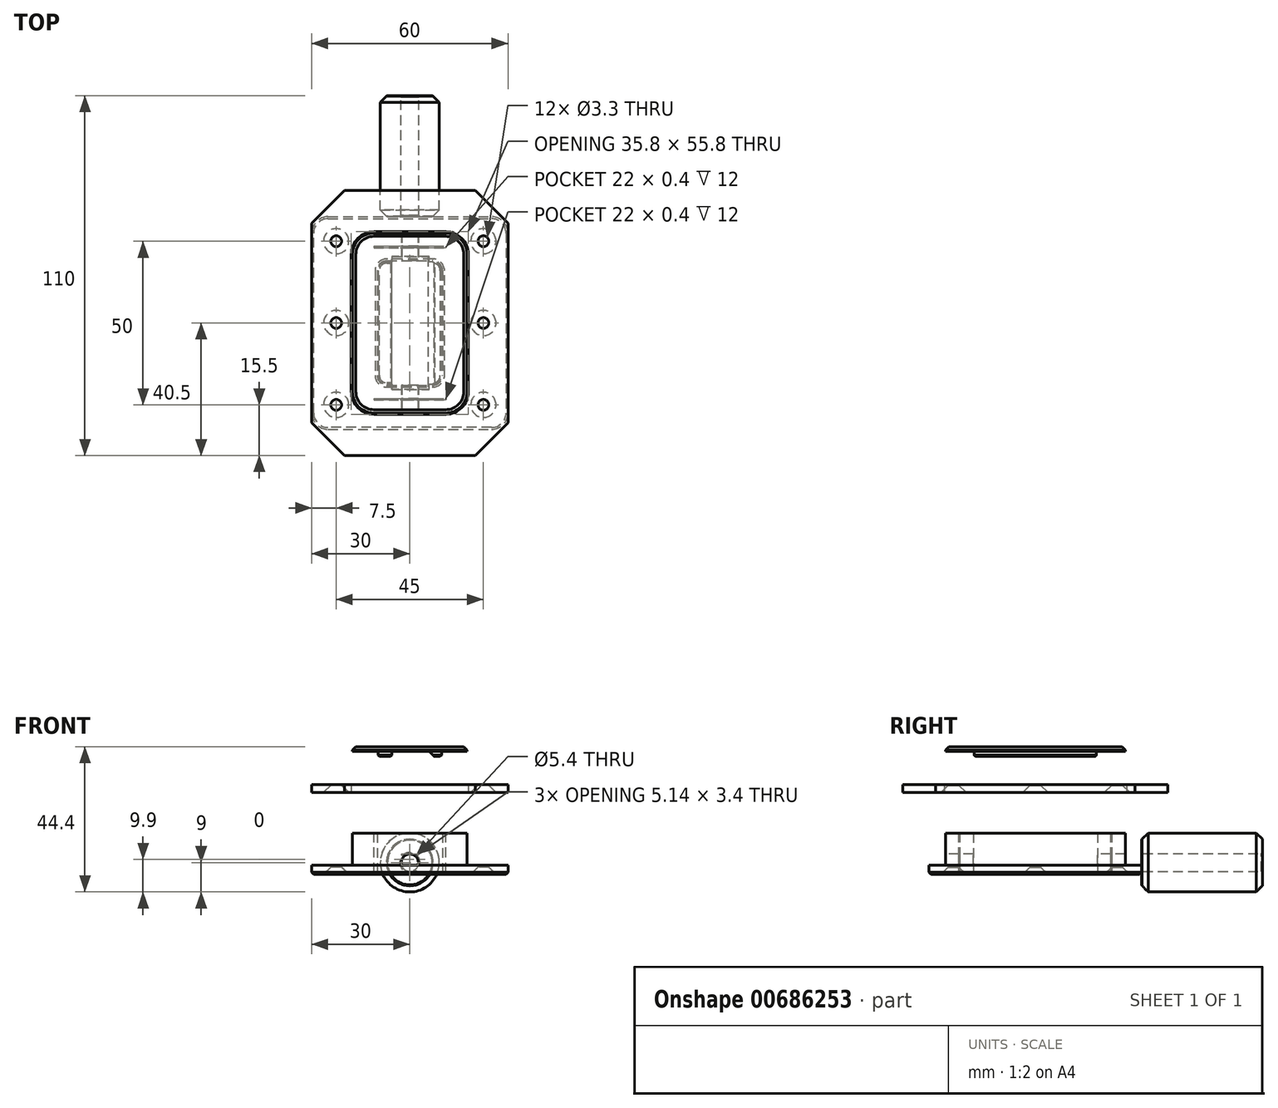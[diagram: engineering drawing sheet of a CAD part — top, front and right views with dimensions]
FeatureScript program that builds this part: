
annotation { "Feature Type Name" : "Feature", "Feature Type Description" : "" }
export const myFeature = defineFeature(function(context is Context, id is Id, definition is map)
    precondition{}
    {
        {
            var Q0;
            Q0=qCreatedBy(makeId("Top.planeOp"),FACE);
            cPlane(context, id + "F0", {"entities" : qUnion([Q0]), "cplaneType" : CPlaneType.OFFSET, "offset" : 25 * mm, "width" : 150 * mm, "height" : 150 * mm});
        }
        {
            var Q0;
            Q0=qCreatedBy(makeId("Top.planeOp"),FACE);
            var sketch = newSketch(context, id + "F1", { "sketchPlane" : qUnion([Q0])});
            skLineSegment(sketch, "E0.bottom", {"start": v(-25, 32.5) * mm, "end": v(25, 32.5) * mm});
            skLineSegment(sketch, "E0.top", {"start": v(-25, -32.5) * mm, "end": v(25, -32.5) * mm});
            skLineSegment(sketch, "E0.left", {"start": v(-30, 27.5) * mm, "end": v(-30, -27.5) * mm});
            skLineSegment(sketch, "E0.right", {"start": v(30, 27.5) * mm, "end": v(30, -27.5) * mm});
            skPoint(sketch, "E1.visualSharp", {"position": v(-30, 32.5) * mm});
            skArc(sketch, "E1.filletArc", {"start": v(-25, 32.5) * mm, "mid": v(-28.54, 31.04) * mm, "end": v(-30, 27.5) * mm});
            skPoint(sketch, "E2.visualSharp", {"position": v(30, 32.5) * mm});
            skArc(sketch, "E2.filletArc", {"start": v(30, 27.5) * mm, "mid": v(28.54, 31.04) * mm, "end": v(25, 32.5) * mm});
            skPoint(sketch, "E3.visualSharp", {"position": v(-30, -32.5) * mm});
            skArc(sketch, "E3.filletArc", {"start": v(-30, -27.5) * mm, "mid": v(-28.54, -31.04) * mm, "end": v(-25, -32.5) * mm});
            skPoint(sketch, "E4.visualSharp", {"position": v(30, -32.5) * mm});
            skArc(sketch, "E4.filletArc", {"start": v(25, -32.5) * mm, "mid": v(28.54, -31.04) * mm, "end": v(30, -27.5) * mm});
            skLineSegment(sketch, "E5.bottom", {"start": v(-7, 19) * mm, "end": v(7, 19) * mm});
            skLineSegment(sketch, "E5.top", {"start": v(-7, -19) * mm, "end": v(7, -19) * mm});
            skLineSegment(sketch, "E5.left", {"start": v(-10, 16) * mm, "end": v(-10, -16) * mm});
            skLineSegment(sketch, "E5.right", {"start": v(10, 16) * mm, "end": v(10, -16) * mm});
            skLineSegment(sketch, "E6", {"start": v(0, 19) * mm, "end": v(0, 32.5) * mm, "construction": true});
            skLineSegment(sketch, "E7", {"start": v(0, -19) * mm, "end": v(0, -32.5) * mm, "construction": true});
            skPoint(sketch, "E8.visualSharp", {"position": v(-10, 19) * mm});
            skArc(sketch, "E8.filletArc", {"start": v(-7, 19) * mm, "mid": v(-9.12, 18.12) * mm, "end": v(-10, 16) * mm});
            skPoint(sketch, "E9.visualSharp", {"position": v(10, 19) * mm});
            skArc(sketch, "E9.filletArc", {"start": v(10, 16) * mm, "mid": v(9.12, 18.12) * mm, "end": v(7, 19) * mm});
            skPoint(sketch, "E10.visualSharp", {"position": v(10, -19) * mm});
            skArc(sketch, "E10.filletArc", {"start": v(7, -19) * mm, "mid": v(9.12, -18.12) * mm, "end": v(10, -16) * mm});
            skPoint(sketch, "E11.visualSharp", {"position": v(-10, -19) * mm});
            skArc(sketch, "E11.filletArc", {"start": v(-10, -16) * mm, "mid": v(-9.12, -18.12) * mm, "end": v(-7, -19) * mm});
            skLineSegment(sketch, "E12", {"start": v(-30, 32.5) * mm, "end": v(30, -32.5) * mm, "construction": true});
            skLineSegment(sketch, "E13", {"start": v(30, 32.5) * mm, "end": v(-30, -32.5) * mm, "construction": true});
            skCircle(sketch, "E14", {"center": v(-22.5, 25) * mm, "radius": 1.65 * mm});
            skCircle(sketch, "E15", {"center": v(22.5, 25) * mm, "radius": 1.65 * mm});
            skCircle(sketch, "E16", {"center": v(22.5, -25) * mm, "radius": 1.65 * mm});
            skCircle(sketch, "E17", {"center": v(-22.5, -25) * mm, "radius": 1.65 * mm});
            skCircle(sketch, "E18", {"center": v(-22.5, 0) * mm, "radius": 1.65 * mm});
            skCircle(sketch, "E19", {"center": v(22.5, 0) * mm, "radius": 1.65 * mm});
            skLineSegment(sketch, "E20.bottom", {"start": v(-22.5, -25) * mm, "end": v(22.5, -25) * mm, "construction": true});
            skLineSegment(sketch, "E20.top", {"start": v(-22.5, 25) * mm, "end": v(22.5, 25) * mm, "construction": true});
            skLineSegment(sketch, "E20.left", {"start": v(-22.5, -25) * mm, "end": v(-22.5, 25) * mm, "construction": true});
            skLineSegment(sketch, "E20.right", {"start": v(22.5, -25) * mm, "end": v(22.5, 25) * mm, "construction": true});
            skLineSegment(sketch, "E21", {"start": v(-22.5, 0) * mm, "end": v(22.5, 0) * mm, "construction": true});
            skSolve(sketch);
        }
        {
            var Q0;
            Q0=makeQuery(id+"F1.imprint","IMPRINT",FACE,{"disambiguationData":[TD([[makeQuery(id+"F1.imprint","IMPRINT",EDGE,{"derivedFrom":sQuery(id+"F1.wireOp",EDGE,"E0.bottom")}),-1.0]])]});
            extrude(context, id + "F2", {"entities" : qUnion([Q0]), "depth" : 2.8 * mm, "offsetDistance" : 25 * mm});
        }
        {
            var Q0;
            Q0=makeQuery(id+"F2.opExtrude","CAP_FACE",FACE,{"disambiguationData":[OSD([sQuery(id+"F1.wireOp",EDGE,"E0.bottom"),sQuery(id+"F1.wireOp",EDGE,"E0.top"),sQuery(id+"F1.wireOp",EDGE,"E0.left"),sQuery(id+"F1.wireOp",EDGE,"E0.right"),sQuery(id+"F1.wireOp",EDGE,"E1.filletArc"),sQuery(id+"F1.wireOp",EDGE,"E2.filletArc"),sQuery(id+"F1.wireOp",EDGE,"E3.filletArc"),sQuery(id+"F1.wireOp",EDGE,"E4.filletArc")])],"isStart":false});
            var sketch = newSketch(context, id + "F3", { "sketchPlane" : qUnion([Q0])});
            skArc(sketch, "E22.0.0", {"start": v(-30, -27.5) * mm, "mid": v(-28.54, -31.04) * mm, "end": v(-25, -32.5) * mm, "construction": true});
            skLineSegment(sketch, "E22.0.1", {"start": v(-25, -32.5) * mm, "end": v(25, -32.5) * mm, "construction": true});
            skArc(sketch, "E22.0.2", {"start": v(25, -32.5) * mm, "mid": v(28.54, -31.04) * mm, "end": v(30, -27.5) * mm, "construction": true});
            skLineSegment(sketch, "E22.0.3", {"start": v(30, -27.5) * mm, "end": v(30, 27.5) * mm, "construction": true});
            skArc(sketch, "E22.0.4", {"start": v(30, 27.5) * mm, "mid": v(28.54, 31.04) * mm, "end": v(25, 32.5) * mm, "construction": true});
            skLineSegment(sketch, "E22.0.5", {"start": v(25, 32.5) * mm, "end": v(-25, 32.5) * mm, "construction": true});
            skArc(sketch, "E22.0.6", {"start": v(-25, 32.5) * mm, "mid": v(-28.54, 31.04) * mm, "end": v(-30, 27.5) * mm, "construction": true});
            skLineSegment(sketch, "E22.0.7", {"start": v(-30, 27.5) * mm, "end": v(-30, -27.5) * mm, "construction": true});
            skLineSegment(sketch, "E23.bottom", {"start": v(-11, 27.5) * mm, "end": v(11, 27.5) * mm});
            skLineSegment(sketch, "E23.top", {"start": v(-11, -27.5) * mm, "end": v(11, -27.5) * mm});
            skLineSegment(sketch, "E23.left", {"start": v(-17.5, 21) * mm, "end": v(-17.5, -21) * mm});
            skLineSegment(sketch, "E23.right", {"start": v(17.5, 21) * mm, "end": v(17.5, -21) * mm});
            skLineSegment(sketch, "E24", {"start": v(0, 32.5) * mm, "end": v(0, 27.5) * mm, "construction": true});
            skLineSegment(sketch, "E25", {"start": v(0, -27.5) * mm, "end": v(0, -32.5) * mm, "construction": true});
            skPoint(sketch, "E26.visualSharp", {"position": v(-17.5, 27.5) * mm});
            skArc(sketch, "E26.filletArc", {"start": v(-11, 27.5) * mm, "mid": v(-15.6, 25.6) * mm, "end": v(-17.5, 21) * mm});
            skPoint(sketch, "E27.visualSharp", {"position": v(17.5, 27.5) * mm});
            skArc(sketch, "E27.filletArc", {"start": v(17.5, 21) * mm, "mid": v(15.6, 25.6) * mm, "end": v(11, 27.5) * mm});
            skPoint(sketch, "E28.visualSharp", {"position": v(-17.5, -27.5) * mm});
            skArc(sketch, "E28.filletArc", {"start": v(-17.5, -21) * mm, "mid": v(-15.6, -25.6) * mm, "end": v(-11, -27.5) * mm});
            skPoint(sketch, "E29.visualSharp", {"position": v(17.5, -27.5) * mm});
            skArc(sketch, "E29.filletArc", {"start": v(11, -27.5) * mm, "mid": v(15.6, -25.6) * mm, "end": v(17.5, -21) * mm});
            skSolve(sketch);
        }
        {
            var Q0;
            Q0=makeQuery(id+"F3.imprint","IMPRINT",FACE,{"disambiguationData":[TD([[makeQuery(id+"F3.imprint","IMPRINT",EDGE,{"derivedFrom":sQuery(id+"F3.wireOp",EDGE,"E23.bottom")}),-1.0]])]});
            extrude(context, id + "F4", {"entities" : qUnion([Q0]), "operationType" : NewBodyOperationType.ADD, "depth" : 9.8 * mm, "offsetDistance" : 25 * mm});
        }
        {
            var Q0;
            Q0=makeQuery(id+"F2.opExtrude","SWEPT_FACE",FACE,{"disambiguationData":[OSD([sQuery(id+"F1.wireOp",EDGE,"E0.top")])]});
            var sketch = newSketch(context, id + "F5", { "sketchPlane" : qUnion([Q0])});
            skLineSegment(sketch, "E30.0.0", {"start": v(-11, 2.8) * mm, "end": v(11, 2.8) * mm, "construction": true});
            skLineSegment(sketch, "E30.0.1", {"start": v(11, 2.8) * mm, "end": v(11, 12.6) * mm, "construction": true});
            skLineSegment(sketch, "E30.0.2", {"start": v(11, 12.6) * mm, "end": v(-11, 12.6) * mm});
            skLineSegment(sketch, "E30.0.3", {"start": v(-11, 12.6) * mm, "end": v(-11, 2.8) * mm, "construction": true});
            skLineSegment(sketch, "E31", {"start": v(-11, 3.6) * mm, "end": v(11, 3.6) * mm});
            skCircle(sketch, "E32", {"center": v(0, 3.6) * mm, "radius": 2.6 * mm});
            skCircle(sketch, "E33", {"center": v(0, 3.6) * mm, "radius": 9 * mm, "construction": true});
            skSolve(sketch);
        }
        {
            var Q0;
            {var subQ0=sQuery(id+"F5.wireOp",EDGE,"E32");var subQ1=sQuery(id+"F5.wireOp",EDGE,"E31");var subQ2=makeQuery(id+"F5.imprint","INTERSECT",VERTEX,{"disambiguationData":[OD(0.0)],"derivedFrom":[subQ1,subQ0]});Q0=makeQuery(id+"F5.imprint","IMPRINT",FACE,{"disambiguationData":[TD([[makeQuery(id+"F5.imprint","IMPRINT",EDGE,{"disambiguationData":[TD([[subQ2,-1.0]])],"derivedFrom":subQ1}),1.0]])]});}
            var Q1;
            {var subQ0=sQuery(id+"F5.wireOp",EDGE,"E32");var subQ1=sQuery(id+"F5.wireOp",EDGE,"E31");var subQ2=makeQuery(id+"F5.imprint","INTERSECT",VERTEX,{"disambiguationData":[OD(0.0)],"derivedFrom":[subQ1,subQ0]});Q1=makeQuery(id+"F5.imprint","IMPRINT",FACE,{"disambiguationData":[TD([[makeQuery(id+"F5.imprint","IMPRINT",EDGE,{"disambiguationData":[TD([[subQ2,-1.0]])],"derivedFrom":subQ1}),-1.0]])]});}
            var Q2;
            {var subQ0=sQuery(id+"F5.wireOp",EDGE,"E32");var subQ1=makeQuery(id+"F2.opExtrude","CAP_EDGE",EDGE,{"disambiguationData":[OSD([sQuery(id+"F1.wireOp",EDGE,"E0.top")])],"isStart":false});var subQ2=makeQuery(id+"F5.imprint","INTERSECT",VERTEX,{"disambiguationData":[OD(0.0)],"derivedFrom":[subQ1,subQ0]});Q2=makeQuery(id+"F5.imprint","IMPRINT",FACE,{"disambiguationData":[TD([[makeQuery(id+"F5.imprint","IMPRINT",EDGE,{"disambiguationData":[TD([[subQ2,-1.0]])],"derivedFrom":subQ0}),1.0]])]});}
            var Q3;
            Q3=makeQuery(id+"F2.opExtrude","SWEPT_FACE",FACE,{"disambiguationData":[OSD([sQuery(id+"F1.wireOp",EDGE,"E0.bottom")])]});
            extrude(context, id + "F6", {"entities" : qUnion([Q0, Q1, Q2]), "operationType" : NewBodyOperationType.REMOVE, "endBound" : BoundingType.UP_TO_SURFACE, "oppositeDirection" : true, "depth" : 25 * mm, "endBoundEntityFace" : qUnion([Q3]), "offsetDistance" : 25 * mm});
        }
        {
            var Q0;
            Q0=qCreatedBy(id+"F0.planeOp",FACE);
            var sketch = newSketch(context, id + "F7", { "sketchPlane" : qUnion([Q0])});
            skArc(sketch, "E34.0", {"start": v(25, -32.5) * mm, "mid": v(28.54, -31.04) * mm, "end": v(30, -27.5) * mm, "construction": true});
            skLineSegment(sketch, "E35.0", {"start": v(30, 27.5) * mm, "end": v(30, -27.5) * mm, "construction": true});
            skLineSegment(sketch, "E36.0", {"start": v(-25, -32.5) * mm, "end": v(25, -32.5) * mm, "construction": true});
            skLineSegment(sketch, "E37.0", {"start": v(-30, 27.5) * mm, "end": v(-30, -27.5) * mm, "construction": true});
            skArc(sketch, "E38.0", {"start": v(-30, -27.5) * mm, "mid": v(-28.54, -31.04) * mm, "end": v(-25, -32.5) * mm, "construction": true});
            skArc(sketch, "E38.1", {"start": v(-25, 32.5) * mm, "mid": v(-28.54, 31.04) * mm, "end": v(-30, 27.5) * mm, "construction": true});
            skLineSegment(sketch, "E38.2", {"start": v(-25, 32.5) * mm, "end": v(25, 32.5) * mm, "construction": true});
            skArc(sketch, "E39.0", {"start": v(30, 27.5) * mm, "mid": v(28.54, 31.04) * mm, "end": v(25, 32.5) * mm, "construction": true});
            skCircle(sketch, "E40.0", {"center": v(22.5, -25) * mm, "radius": 1.65 * mm});
            skCircle(sketch, "E41.0", {"center": v(22.5, 0) * mm, "radius": 1.65 * mm});
            skCircle(sketch, "E42.0", {"center": v(22.5, 25) * mm, "radius": 1.65 * mm});
            skCircle(sketch, "E43.0", {"center": v(-22.5, 25) * mm, "radius": 1.65 * mm});
            skCircle(sketch, "E44.0", {"center": v(-22.5, 0) * mm, "radius": 1.65 * mm});
            skCircle(sketch, "E45.0", {"center": v(-22.5, -25) * mm, "radius": 1.65 * mm});
            skArc(sketch, "E46.0", {"start": v(11, -27.5) * mm, "mid": v(15.6, -25.6) * mm, "end": v(17.5, -21) * mm, "construction": true});
            skLineSegment(sketch, "E47.0", {"start": v(17.5, 21) * mm, "end": v(17.5, -21) * mm, "construction": true});
            skArc(sketch, "E48.0", {"start": v(17.5, 21) * mm, "mid": v(15.6, 25.6) * mm, "end": v(11, 27.5) * mm, "construction": true});
            skLineSegment(sketch, "E49.0", {"start": v(-11, 27.5) * mm, "end": v(11, 27.5) * mm, "construction": true});
            skArc(sketch, "E50.0", {"start": v(-11, 27.5) * mm, "mid": v(-15.6, 25.6) * mm, "end": v(-17.5, 21) * mm, "construction": true});
            skLineSegment(sketch, "E51.0", {"start": v(-17.5, 21) * mm, "end": v(-17.5, -21) * mm, "construction": true});
            skArc(sketch, "E52.0", {"start": v(-17.5, -21) * mm, "mid": v(-15.6, -25.6) * mm, "end": v(-11, -27.5) * mm, "construction": true});
            skLineSegment(sketch, "E53.0", {"start": v(-11, -27.5) * mm, "end": v(11, -27.5) * mm, "construction": true});
            skLineSegment(sketch, "E54.bottom", {"start": v(30, -40.5) * mm, "end": v(-30, -40.5) * mm});
            skLineSegment(sketch, "E54.top", {"start": v(30, 40.5) * mm, "end": v(-30, 40.5) * mm});
            skLineSegment(sketch, "E54.left", {"start": v(30, -40.5) * mm, "end": v(30, 40.5) * mm});
            skLineSegment(sketch, "E54.right", {"start": v(-30, -40.5) * mm, "end": v(-30, 40.5) * mm});
            skArc(sketch, "E55.0", {"start": v(-11, 27.9) * mm, "mid": v(-15.88, 25.88) * mm, "end": v(-17.9, 21) * mm});
            skLineSegment(sketch, "E55.1", {"start": v(-11, 27.9) * mm, "end": v(11, 27.9) * mm});
            skLineSegment(sketch, "E55.2", {"start": v(-17.9, 21) * mm, "end": v(-17.9, -21) * mm});
            skArc(sketch, "E55.3", {"start": v(17.9, 21) * mm, "mid": v(15.88, 25.88) * mm, "end": v(11, 27.9) * mm});
            skArc(sketch, "E55.4", {"start": v(-17.9, -21) * mm, "mid": v(-15.88, -25.88) * mm, "end": v(-11, -27.9) * mm});
            skLineSegment(sketch, "E55.5", {"start": v(-11, -27.9) * mm, "end": v(11, -27.9) * mm});
            skArc(sketch, "E55.6", {"start": v(11, -27.9) * mm, "mid": v(15.88, -25.88) * mm, "end": v(17.9, -21) * mm});
            skLineSegment(sketch, "E55.7", {"start": v(17.9, 21) * mm, "end": v(17.9, -21) * mm});
            skSolve(sketch);
        }
        {
            var Q0;
            Q0=makeQuery(id+"F7.imprint","IMPRINT",FACE,{"disambiguationData":[TD([[makeQuery(id+"F7.imprint","IMPRINT",EDGE,{"derivedFrom":sQuery(id+"F7.wireOp",EDGE,"E40.0")}),-1.0]])]});
            extrude(context, id + "F8", {"entities" : qUnion([Q0]), "depth" : 2.4 * mm, "offsetDistance" : 25 * mm});
        }
        {
            var Q0;
            Q0=makeQuery(id+"F8.opExtrude","SWEPT_EDGE",EDGE,{"disambiguationData":[OSD([sQuery(id+"F7.wireOp",EDGE,"E54.bottom"),sQuery(id+"F7.wireOp",EDGE,"E54.left")])]});
            var Q1;
            Q1=makeQuery(id+"F8.opExtrude","SWEPT_EDGE",EDGE,{"disambiguationData":[OSD([sQuery(id+"F7.wireOp",EDGE,"E54.top"),sQuery(id+"F7.wireOp",EDGE,"E54.left")])]});
            var Q2;
            Q2=makeQuery(id+"F8.opExtrude","SWEPT_EDGE",EDGE,{"disambiguationData":[OSD([sQuery(id+"F7.wireOp",EDGE,"E54.top"),sQuery(id+"F7.wireOp",EDGE,"E54.right")])]});
            var Q3;
            Q3=makeQuery(id+"F8.opExtrude","SWEPT_EDGE",EDGE,{"disambiguationData":[OSD([sQuery(id+"F7.wireOp",EDGE,"E54.bottom"),sQuery(id+"F7.wireOp",EDGE,"E54.right")])]});
            chamfer(context, id + "F9", {"entities" : qUnion([Q0, Q1, Q2, Q3]), "width" : 10 * mm, "tangentPropagation" : true});
        }
        {
            var Q0;
            Q0=makeQuery(id+"F2.opExtrude","CAP_EDGE",EDGE,{"disambiguationData":[OSD([sQuery(id+"F1.wireOp",EDGE,"E17")])],"isStart":true});
            var Q1;
            Q1=makeQuery(id+"F2.opExtrude","CAP_EDGE",EDGE,{"disambiguationData":[OSD([sQuery(id+"F1.wireOp",EDGE,"E14")])],"isStart":true});
            var Q2;
            Q2=makeQuery(id+"F2.opExtrude","CAP_EDGE",EDGE,{"disambiguationData":[OSD([sQuery(id+"F1.wireOp",EDGE,"E15")])],"isStart":true});
            var Q3;
            Q3=makeQuery(id+"F2.opExtrude","CAP_EDGE",EDGE,{"disambiguationData":[OSD([sQuery(id+"F1.wireOp",EDGE,"E16")])],"isStart":true});
            var Q4;
            Q4=makeQuery(id+"F2.opExtrude","CAP_EDGE",EDGE,{"disambiguationData":[OSD([sQuery(id+"F1.wireOp",EDGE,"E19")])],"isStart":true});
            var Q5;
            Q5=makeQuery(id+"F2.opExtrude","CAP_EDGE",EDGE,{"disambiguationData":[OSD([sQuery(id+"F1.wireOp",EDGE,"E18")])],"isStart":true});
            var Q6;
            Q6=makeQuery(id+"F8.opExtrude","CAP_EDGE",EDGE,{"disambiguationData":[OSD([sQuery(id+"F7.wireOp",EDGE,"E40.0")])],"isStart":true});
            var Q7;
            Q7=makeQuery(id+"F8.opExtrude","CAP_EDGE",EDGE,{"disambiguationData":[OSD([sQuery(id+"F7.wireOp",EDGE,"E41.0")])],"isStart":true});
            var Q8;
            Q8=makeQuery(id+"F8.opExtrude","CAP_EDGE",EDGE,{"disambiguationData":[OSD([sQuery(id+"F7.wireOp",EDGE,"E42.0")])],"isStart":true});
            var Q9;
            Q9=makeQuery(id+"F8.opExtrude","CAP_EDGE",EDGE,{"disambiguationData":[OSD([sQuery(id+"F7.wireOp",EDGE,"E43.0")])],"isStart":true});
            var Q10;
            Q10=makeQuery(id+"F8.opExtrude","CAP_EDGE",EDGE,{"disambiguationData":[OSD([sQuery(id+"F7.wireOp",EDGE,"E44.0")])],"isStart":true});
            var Q11;
            Q11=makeQuery(id+"F8.opExtrude","CAP_EDGE",EDGE,{"disambiguationData":[OSD([sQuery(id+"F7.wireOp",EDGE,"E45.0")])],"isStart":true});
            chamfer(context, id + "F10", {"entities" : qUnion([Q0, Q1, Q2, Q3, Q4, Q5, Q6, Q7, Q8, Q9, Q10, Q11]), "width" : 2.2 * mm, "tangentPropagation" : true});
        }
        {
            var Q0;
            {var subQ0=sQuery(id+"F1.wireOp",EDGE,"E5.bottom");Q0=makeQuery(id+"F4.boolean.opBoolean","MERGE",FACE,{"derivedFrom":[makeQuery(id+"F2.opExtrude","SWEPT_FACE",FACE,{"disambiguationData":[OSD([subQ0])]}),makeQuery(id+"F4.opExtrude","SWEPT_FACE",FACE,{"disambiguationData":[OSD([subQ0])]})]});}
            cPlane(context, id + "F11", {"entities" : qUnion([Q0]), "cplaneType" : CPlaneType.OFFSET, "offset" : 50.5 * mm, "oppositeDirection" : true, "width" : 150 * mm, "height" : 150 * mm});
        }
        {
            var Q0;
            Q0=qCreatedBy(id+"F11.planeOp",FACE);
            var sketch = newSketch(context, id + "F12", { "sketchPlane" : qUnion([Q0])});
            skCircle(sketch, "E56.0", {"center": v(0, 3.6) * mm, "radius": 2.6 * mm, "construction": true});
            skCircle(sketch, "E57", {"center": v(0, 3.6) * mm, "radius": 9 * mm});
            skCircle(sketch, "E58", {"center": v(0, 3.6) * mm, "radius": 2.7 * mm});
            skSolve(sketch);
        }
        {
            var Q0;
            Q0=makeQuery(id+"F12.imprint","IMPRINT",FACE,{"disambiguationData":[TD([[makeQuery(id+"F12.imprint","IMPRINT",EDGE,{"derivedFrom":sQuery(id+"F12.wireOp",EDGE,"E57")}),1.0]])]});
            extrude(context, id + "F13", {"entities" : qUnion([Q0]), "depth" : 37 * mm, "offsetDistance" : 25 * mm});
        }
        {
            var Q0;
            Q0=makeQuery(id+"F13.opExtrude","CAP_EDGE",EDGE,{"disambiguationData":[OSD([sQuery(id+"F12.wireOp",EDGE,"E57")])],"isStart":true});
            var Q1;
            Q1=makeQuery(id+"F13.opExtrude","CAP_EDGE",EDGE,{"disambiguationData":[OSD([sQuery(id+"F12.wireOp",EDGE,"E57")])],"isStart":false});
            chamfer(context, id + "F14", {"entities" : qUnion([Q0, Q1]), "width" : 2 * mm, "tangentPropagation" : true});
        }
        {
            var Q0;
            Q0=makeQuery(id+"F13.opExtrude","CAP_FACE",FACE,{"disambiguationData":[OSD([sQuery(id+"F12.wireOp",EDGE,"E56.0"),sQuery(id+"F12.wireOp",EDGE,"E57")])],"isStart":true});
            var Q1;
            Q1=makeQuery(id+"F13.opExtrude","CAP_FACE",FACE,{"disambiguationData":[OSD([sQuery(id+"F12.wireOp",EDGE,"E56.0"),sQuery(id+"F12.wireOp",EDGE,"E57")])],"isStart":false});
            chamfer(context, id + "F15", {"entities" : qUnion([Q0, Q1]), "width" : .4 * mm, "tangentPropagation" : true});
        }
        {
            var Q0;
            Q0=makeQuery(id+"F2.opExtrude","CAP_EDGE",EDGE,{"disambiguationData":[OSD([sQuery(id+"F1.wireOp",EDGE,"E0.top")])],"isStart":true});
            var Q1;
            Q1=makeQuery(id+"F2.opExtrude","CAP_EDGE",EDGE,{"disambiguationData":[OSD([sQuery(id+"F1.wireOp",EDGE,"E5.left")])],"isStart":true});
            chamfer(context, id + "F16", {"entities" : qUnion([Q0, Q1]), "width" : .6 * mm, "tangentPropagation" : true});
        }
        {
            var Q0;
            Q0=makeQuery(id+"F4.opExtrude","CAP_FACE",FACE,{"disambiguationData":[OSD([sQuery(id+"F1.wireOp",EDGE,"E5.bottom"),sQuery(id+"F1.wireOp",EDGE,"E5.top"),sQuery(id+"F1.wireOp",EDGE,"E5.left"),sQuery(id+"F1.wireOp",EDGE,"E5.right"),sQuery(id+"F1.wireOp",EDGE,"E8.filletArc"),sQuery(id+"F1.wireOp",EDGE,"E9.filletArc"),sQuery(id+"F1.wireOp",EDGE,"E10.filletArc"),sQuery(id+"F1.wireOp",EDGE,"E11.filletArc"),sQuery(id+"F3.wireOp",EDGE,"E23.bottom"),sQuery(id+"F3.wireOp",EDGE,"E23.top"),sQuery(id+"F3.wireOp",EDGE,"E23.left"),sQuery(id+"F3.wireOp",EDGE,"E23.right"),sQuery(id+"F3.wireOp",EDGE,"E26.filletArc"),sQuery(id+"F3.wireOp",EDGE,"E27.filletArc"),sQuery(id+"F3.wireOp",EDGE,"E28.filletArc"),sQuery(id+"F3.wireOp",EDGE,"E29.filletArc")])],"isStart":false});
            cPlane(context, id + "F17", {"entities" : qUnion([Q0]), "cplaneType" : CPlaneType.OFFSET, "offset" : 25 * mm, "width" : 150 * mm, "height" : 150 * mm});
        }
        {
            var Q0;
            Q0=qCreatedBy(id+"F17.planeOp",FACE);
            var sketch = newSketch(context, id + "F18", { "sketchPlane" : qUnion([Q0])});
            skArc(sketch, "E59.0.0", {"start": v(-17.5, -21) * mm, "mid": v(-15.6, -25.6) * mm, "end": v(-11, -27.5) * mm});
            skLineSegment(sketch, "E59.0.1", {"start": v(-11, -27.5) * mm, "end": v(11, -27.5) * mm});
            skArc(sketch, "E59.0.2", {"start": v(11, -27.5) * mm, "mid": v(15.6, -25.6) * mm, "end": v(17.5, -21) * mm});
            skLineSegment(sketch, "E59.0.3", {"start": v(17.5, -21) * mm, "end": v(17.5, 21) * mm});
            skArc(sketch, "E59.0.4", {"start": v(17.5, 21) * mm, "mid": v(15.6, 25.6) * mm, "end": v(11, 27.5) * mm});
            skLineSegment(sketch, "E59.0.5", {"start": v(11, 27.5) * mm, "end": v(-11, 27.5) * mm});
            skArc(sketch, "E59.0.6", {"start": v(-11, 27.5) * mm, "mid": v(-15.6, 25.6) * mm, "end": v(-17.5, 21) * mm});
            skLineSegment(sketch, "E59.0.7", {"start": v(-17.5, 21) * mm, "end": v(-17.5, -21) * mm});
            skSolve(sketch);
        }
        {
            var Q0;
            Q0=qSketchRegion(id+"F18",true);
            extrude(context, id + "F19", {"entities" : qUnion([Q0]), "depth" : 1.4 * mm, "offsetDistance" : 25 * mm});
        }
        {
            var Q0;
            Q0=makeQuery(id+"F19.opExtrude","CAP_FACE",FACE,{"disambiguationData":[OSD([sQuery(id+"F18.wireOp",EDGE,"E59.0.0"),sQuery(id+"F18.wireOp",EDGE,"E59.0.1"),sQuery(id+"F18.wireOp",EDGE,"E59.0.2"),sQuery(id+"F18.wireOp",EDGE,"E59.0.3"),sQuery(id+"F18.wireOp",EDGE,"E59.0.4"),sQuery(id+"F18.wireOp",EDGE,"E59.0.5"),sQuery(id+"F18.wireOp",EDGE,"E59.0.6"),sQuery(id+"F18.wireOp",EDGE,"E59.0.7")])],"isStart":true});
            var sketch = newSketch(context, id + "F20", { "sketchPlane" : qUnion([Q0])});
            skLineSegment(sketch, "E60.0", {"start": v(-10, -16) * mm, "end": v(-10, 16) * mm, "construction": true});
            skArc(sketch, "E61.0", {"start": v(-7, -19) * mm, "mid": v(-9.12, -18.12) * mm, "end": v(-10, -16) * mm, "construction": true});
            skLineSegment(sketch, "E62.0", {"start": v(-7, -19) * mm, "end": v(7, -19) * mm, "construction": true});
            skArc(sketch, "E63.0", {"start": v(10, -16) * mm, "mid": v(9.12, -18.12) * mm, "end": v(7, -19) * mm, "construction": true});
            skLineSegment(sketch, "E64.0", {"start": v(10, -16) * mm, "end": v(10, 16) * mm, "construction": true});
            skArc(sketch, "E65.0", {"start": v(7, 19) * mm, "mid": v(9.12, 18.12) * mm, "end": v(10, 16) * mm, "construction": true});
            skLineSegment(sketch, "E66.0", {"start": v(-7, 19) * mm, "end": v(7, 19) * mm, "construction": true});
            skArc(sketch, "E67.0", {"start": v(-10, 16) * mm, "mid": v(-9.12, 18.12) * mm, "end": v(-7, 19) * mm, "construction": true});
            skArc(sketch, "E68.0", {"start": v(-7, -18.7) * mm, "mid": v(-8.9, -17.9) * mm, "end": v(-9.7, -16) * mm});
            skLineSegment(sketch, "E68.1", {"start": v(-7, -18.7) * mm, "end": v(7, -18.7) * mm});
            skLineSegment(sketch, "E68.2", {"start": v(-9.7, -16) * mm, "end": v(-9.7, 16) * mm});
            skArc(sketch, "E68.3", {"start": v(9.7, -16) * mm, "mid": v(8.9, -17.9) * mm, "end": v(7, -18.7) * mm});
            skArc(sketch, "E68.4", {"start": v(-9.7, 16) * mm, "mid": v(-8.9, 17.9) * mm, "end": v(-7, 18.7) * mm});
            skLineSegment(sketch, "E68.5", {"start": v(-7, 18.7) * mm, "end": v(7, 18.7) * mm});
            skArc(sketch, "E68.6", {"start": v(7, 18.7) * mm, "mid": v(8.9, 17.9) * mm, "end": v(9.7, 16) * mm});
            skLineSegment(sketch, "E68.7", {"start": v(9.7, -16) * mm, "end": v(9.7, 16) * mm});
            skSolve(sketch);
        }
        {
            var Q0;
            Q0=qSketchRegion(id+"F20",true);
            extrude(context, id + "F21", {"entities" : qUnion([Q0]), "operationType" : NewBodyOperationType.ADD, "depth" : 1.6 * mm, "offsetDistance" : 25 * mm});
        }
        {
            var Q0;
            Q0=makeQuery(id+"F21.opExtrude","CAP_FACE",FACE,{"disambiguationData":[OSD([sQuery(id+"F20.wireOp",EDGE,"E68.0"),sQuery(id+"F20.wireOp",EDGE,"E68.1"),sQuery(id+"F20.wireOp",EDGE,"E68.2"),sQuery(id+"F20.wireOp",EDGE,"E68.3"),sQuery(id+"F20.wireOp",EDGE,"E68.4"),sQuery(id+"F20.wireOp",EDGE,"E68.5"),sQuery(id+"F20.wireOp",EDGE,"E68.6"),sQuery(id+"F20.wireOp",EDGE,"E68.7")])],"isStart":false});
            var sketch = newSketch(context, id + "F22", { "sketchPlane" : qUnion([Q0])});
            skLineSegment(sketch, "E69.bottom", {"start": v(-5.5, 20.3) * mm, "end": v(5.5, 20.3) * mm});
            skLineSegment(sketch, "E69.top", {"start": v(-5.5, -20.3) * mm, "end": v(5.5, -20.3) * mm});
            skArc(sketch, "E70.0.0", {"start": v(7, -18.7) * mm, "mid": v(8.9, -17.9) * mm, "end": v(9.7, -16) * mm, "construction": true});
            skLineSegment(sketch, "E70.0.1", {"start": v(9.7, -16) * mm, "end": v(9.7, 16) * mm, "construction": true});
            skArc(sketch, "E70.0.2", {"start": v(9.7, 16) * mm, "mid": v(8.9, 17.9) * mm, "end": v(7, 18.7) * mm, "construction": true});
            skLineSegment(sketch, "E70.0.3", {"start": v(7, 18.7) * mm, "end": v(-7, 18.7) * mm, "construction": true});
            skArc(sketch, "E70.0.4", {"start": v(-7, 18.7) * mm, "mid": v(-8.9, 17.9) * mm, "end": v(-9.7, 16) * mm, "construction": true});
            skLineSegment(sketch, "E70.0.5", {"start": v(-9.7, 16) * mm, "end": v(-9.7, -16) * mm, "construction": true});
            skArc(sketch, "E70.0.6", {"start": v(-9.7, -16) * mm, "mid": v(-8.9, -17.9) * mm, "end": v(-7, -18.7) * mm, "construction": true});
            skLineSegment(sketch, "E70.0.7", {"start": v(-7, -18.7) * mm, "end": v(7, -18.7) * mm, "construction": true});
            skLineSegment(sketch, "E71", {"start": v(0, 20.3) * mm, "end": v(0, 18.7) * mm, "construction": true});
            skLineSegment(sketch, "E72", {"start": v(0, -18.7) * mm, "end": v(0, -20.3) * mm, "construction": true});
            skLineSegment(sketch, "E73", {"start": v(-5.5, 20.3) * mm, "end": v(-5.5, -20.3) * mm});
            skLineSegment(sketch, "E74", {"start": v(5.5, -20.3) * mm, "end": v(5.5, 20.3) * mm});
            skSolve(sketch);
        }
        {
            var Q0;
            {var subQ0=sQuery(id+"F22.wireOp",EDGE,"E73");var subQ1=makeQuery(id+"F21.opExtrude","CAP_EDGE",EDGE,{"disambiguationData":[OSD([sQuery(id+"F20.wireOp",EDGE,"E68.5")])],"isStart":false});var subQ2=makeQuery(id+"F22.imprint","INTERSECT",VERTEX,{"derivedFrom":[subQ1,subQ0]});Q0=makeQuery(id+"F22.imprint","IMPRINT",FACE,{"disambiguationData":[TD([[makeQuery(id+"F22.imprint","IMPRINT",EDGE,{"disambiguationData":[TD([[subQ2,-1.0]])],"derivedFrom":subQ0}),1.0]])]});}
            var Q1;
            {var subQ0=sQuery(id+"F22.wireOp",EDGE,"E69.bottom");Q1=makeQuery(id+"F22.imprint","IMPRINT",FACE,{"disambiguationData":[TD([[makeQuery(id+"F22.imprint","IMPRINT",EDGE,{"derivedFrom":subQ0}),-1.0]])]});}
            var Q2;
            {var subQ0=sQuery(id+"F22.wireOp",EDGE,"E69.top");Q2=makeQuery(id+"F22.imprint","IMPRINT",FACE,{"disambiguationData":[TD([[makeQuery(id+"F22.imprint","IMPRINT",EDGE,{"derivedFrom":subQ0}),1.0]])]});}
            extrude(context, id + "F23", {"entities" : qUnion([Q0, Q1, Q2]), "operationType" : NewBodyOperationType.REMOVE, "oppositeDirection" : true, "depth" : 2 * mm, "offsetDistance" : 25 * mm});
        }
        {
            var Q0;
            Q0=makeQuery(id+"F23.boolean.opBoolean","COPY",EDGE,{"derivedFrom":makeQuery(id+"F23.opExtrude","CAP_EDGE",EDGE,{"disambiguationData":[OSD([sQuery(id+"F22.wireOp",EDGE,"E73")])],"isStart":true})});
            var Q1;
            Q1=makeQuery(id+"F23.boolean.opBoolean","COPY",EDGE,{"derivedFrom":makeQuery(id+"F23.opExtrude","CAP_EDGE",EDGE,{"disambiguationData":[OSD([sQuery(id+"F22.wireOp",EDGE,"E74")])],"isStart":true})});
            chamfer(context, id + "F24", {"entities" : qUnion([Q0, Q1]), "width" : 2 * mm, "tangentPropagation" : true});
        }
        {
            var Q0;
            {var subQ0=sQuery(id+"F20.wireOp",EDGE,"E68.4");var subQ1=sQuery(id+"F20.wireOp",EDGE,"E68.2");var subQ2=sQuery(id+"F20.wireOp",EDGE,"E68.1");var subQ3=sQuery(id+"F20.wireOp",EDGE,"E68.0");var subQ4=sQuery(id+"F20.wireOp",EDGE,"E68.5");Q0=makeQuery(id+"F23.boolean.opBoolean","SPLIT",FACE,{"disambiguationData":[TD([makeQuery(id+"F21.opExtrude","SWEPT_FACE",FACE,{"disambiguationData":[OSD([subQ3])]})])],"derivedFrom":makeQuery(id+"F21.opExtrude","CAP_FACE",FACE,{"disambiguationData":[OSD([subQ3,subQ2,subQ1,sQuery(id+"F20.wireOp",EDGE,"E68.3"),subQ0,subQ4,sQuery(id+"F20.wireOp",EDGE,"E68.6"),sQuery(id+"F20.wireOp",EDGE,"E68.7")])],"isStart":false})});}
            var Q1;
            {var subQ0=sQuery(id+"F20.wireOp",EDGE,"E68.5");var subQ1=sQuery(id+"F20.wireOp",EDGE,"E68.3");var subQ2=sQuery(id+"F20.wireOp",EDGE,"E68.6");var subQ3=sQuery(id+"F20.wireOp",EDGE,"E68.1");var subQ4=sQuery(id+"F20.wireOp",EDGE,"E68.7");Q1=makeQuery(id+"F23.boolean.opBoolean","SPLIT",FACE,{"disambiguationData":[TD([makeQuery(id+"F21.opExtrude","SWEPT_FACE",FACE,{"disambiguationData":[OSD([subQ1])]})])],"derivedFrom":makeQuery(id+"F21.opExtrude","CAP_FACE",FACE,{"disambiguationData":[OSD([sQuery(id+"F20.wireOp",EDGE,"E68.0"),subQ3,sQuery(id+"F20.wireOp",EDGE,"E68.2"),subQ1,sQuery(id+"F20.wireOp",EDGE,"E68.4"),subQ0,subQ2,subQ4])],"isStart":false})});}
            chamfer(context, id + "F25", {"entities" : qUnion([Q0, Q1]), "width" : .4 * mm, "tangentPropagation" : true});
        }
        {
            var Q0;
            Q0=makeQuery(id+"F19.opExtrude","CAP_FACE",FACE,{"disambiguationData":[OSD([sQuery(id+"F18.wireOp",EDGE,"E59.0.0"),sQuery(id+"F18.wireOp",EDGE,"E59.0.1"),sQuery(id+"F18.wireOp",EDGE,"E59.0.2"),sQuery(id+"F18.wireOp",EDGE,"E59.0.3"),sQuery(id+"F18.wireOp",EDGE,"E59.0.4"),sQuery(id+"F18.wireOp",EDGE,"E59.0.5"),sQuery(id+"F18.wireOp",EDGE,"E59.0.6"),sQuery(id+"F18.wireOp",EDGE,"E59.0.7")])],"isStart":false});
            chamfer(context, id + "F26", {"entities" : qUnion([Q0]), "width" : 1 * mm, "tangentPropagation" : true});
        }
        {
            var Q0;
            Q0=makeQuery(id+"F4.opExtrude","CAP_FACE",FACE,{"disambiguationData":[OSD([sQuery(id+"F1.wireOp",EDGE,"E5.bottom"),sQuery(id+"F1.wireOp",EDGE,"E5.top"),sQuery(id+"F1.wireOp",EDGE,"E5.left"),sQuery(id+"F1.wireOp",EDGE,"E5.right"),sQuery(id+"F1.wireOp",EDGE,"E8.filletArc"),sQuery(id+"F1.wireOp",EDGE,"E9.filletArc"),sQuery(id+"F1.wireOp",EDGE,"E10.filletArc"),sQuery(id+"F1.wireOp",EDGE,"E11.filletArc"),sQuery(id+"F3.wireOp",EDGE,"E23.bottom"),sQuery(id+"F3.wireOp",EDGE,"E23.top"),sQuery(id+"F3.wireOp",EDGE,"E23.left"),sQuery(id+"F3.wireOp",EDGE,"E23.right"),sQuery(id+"F3.wireOp",EDGE,"E26.filletArc"),sQuery(id+"F3.wireOp",EDGE,"E27.filletArc"),sQuery(id+"F3.wireOp",EDGE,"E28.filletArc"),sQuery(id+"F3.wireOp",EDGE,"E29.filletArc")])],"isStart":false});
            var sketch = newSketch(context, id + "F27", { "sketchPlane" : qUnion([Q0])});
            skArc(sketch, "E75.0.0", {"start": v(-17.5, -21) * mm, "mid": v(-15.6, -25.6) * mm, "end": v(-11, -27.5) * mm, "construction": true});
            skLineSegment(sketch, "E75.0.1", {"start": v(-11, -27.5) * mm, "end": v(11, -27.5) * mm, "construction": true});
            skArc(sketch, "E75.0.2", {"start": v(11, -27.5) * mm, "mid": v(15.6, -25.6) * mm, "end": v(17.5, -21) * mm, "construction": true});
            skLineSegment(sketch, "E75.0.3", {"start": v(17.5, -21) * mm, "end": v(17.5, 21) * mm, "construction": true});
            skArc(sketch, "E75.0.4", {"start": v(17.5, 21) * mm, "mid": v(15.6, 25.6) * mm, "end": v(11, 27.5) * mm, "construction": true});
            skLineSegment(sketch, "E75.0.5", {"start": v(11, 27.5) * mm, "end": v(-11, 27.5) * mm, "construction": true});
            skArc(sketch, "E75.0.6", {"start": v(-11, 27.5) * mm, "mid": v(-15.6, 25.6) * mm, "end": v(-17.5, 21) * mm, "construction": true});
            skLineSegment(sketch, "E75.0.7", {"start": v(-17.5, 21) * mm, "end": v(-17.5, -21) * mm, "construction": true});
            skLineSegment(sketch, "E76.bottom", {"start": v(-11, 23.45) * mm, "end": v(11, 23.45) * mm});
            skLineSegment(sketch, "E76.top", {"start": v(-11, 23.05) * mm, "end": v(11, 23.05) * mm});
            skLineSegment(sketch, "E76.left", {"start": v(-11, 23.45) * mm, "end": v(-11, 23.05) * mm});
            skLineSegment(sketch, "E76.right", {"start": v(11, 23.45) * mm, "end": v(11, 23.05) * mm});
            skLineSegment(sketch, "E77", {"start": v(-11, 27.5) * mm, "end": v(-11, -27.5) * mm, "construction": true});
            skLineSegment(sketch, "E78", {"start": v(11, -27.5) * mm, "end": v(11, 27.5) * mm, "construction": true});
            skLineSegment(sketch, "E79", {"start": v(0, 27.5) * mm, "end": v(0, 23.45) * mm, "construction": true});
            skLineSegment(sketch, "E80", {"start": v(0, 19) * mm, "end": v(0, 23.05) * mm, "construction": true});
            skLineSegment(sketch, "E81", {"start": v(0, -19) * mm, "end": v(0, -23.05) * mm, "construction": true});
            skLineSegment(sketch, "E82", {"start": v(0, -27.5) * mm, "end": v(0, -23.45) * mm, "construction": true});
            skLineSegment(sketch, "E83.bottom", {"start": v(-11, -23.05) * mm, "end": v(11, -23.05) * mm});
            skLineSegment(sketch, "E83.top", {"start": v(-11, -23.45) * mm, "end": v(11, -23.45) * mm});
            skLineSegment(sketch, "E83.left", {"start": v(-11, -23.05) * mm, "end": v(-11, -23.45) * mm});
            skLineSegment(sketch, "E83.right", {"start": v(11, -23.05) * mm, "end": v(11, -23.45) * mm});
            skSolve(sketch);
        }
        {
            var Q0;
            Q0=makeQuery(id+"F27.imprint","IMPRINT",FACE,{"disambiguationData":[TD([[makeQuery(id+"F27.imprint","IMPRINT",EDGE,{"derivedFrom":sQuery(id+"F27.wireOp",EDGE,"E76.bottom")}),-1.0]])]});
            var Q1;
            Q1=makeQuery(id+"F27.imprint","IMPRINT",FACE,{"disambiguationData":[TD([[makeQuery(id+"F27.imprint","IMPRINT",EDGE,{"derivedFrom":sQuery(id+"F27.wireOp",EDGE,"E83.bottom")}),-1.0]])]});
            var Q2;
            {var subQ0=sQuery(id+"F1.wireOp",EDGE,"E2.filletArc");var subQ1=sQuery(id+"F1.wireOp",EDGE,"E19");var subQ2=sQuery(id+"F1.wireOp",EDGE,"E0.bottom");var subQ3=sQuery(id+"F1.wireOp",EDGE,"E15");var subQ4=sQuery(id+"F1.wireOp",EDGE,"E16");var subQ5=sQuery(id+"F1.wireOp",EDGE,"E4.filletArc");var subQ6=sQuery(id+"F1.wireOp",EDGE,"E0.right");var subQ7=sQuery(id+"F1.wireOp",EDGE,"E0.top");Q2=makeQuery(id+"F6.boolean.opBoolean","SPLIT",FACE,{"disambiguationData":[TD([makeQuery(id+"F2.opExtrude","SWEPT_FACE",FACE,{"disambiguationData":[OSD([subQ6])]})])],"derivedFrom":makeQuery(id+"F2.opExtrude","CAP_FACE",FACE,{"disambiguationData":[OSD([subQ2,subQ7,sQuery(id+"F1.wireOp",EDGE,"E0.left"),subQ6,sQuery(id+"F1.wireOp",EDGE,"E1.filletArc"),subQ0,sQuery(id+"F1.wireOp",EDGE,"E3.filletArc"),subQ5,sQuery(id+"F1.wireOp",EDGE,"E5.bottom"),sQuery(id+"F1.wireOp",EDGE,"E5.top"),sQuery(id+"F1.wireOp",EDGE,"E5.left"),sQuery(id+"F1.wireOp",EDGE,"E5.right"),sQuery(id+"F1.wireOp",EDGE,"E8.filletArc"),sQuery(id+"F1.wireOp",EDGE,"E9.filletArc"),sQuery(id+"F1.wireOp",EDGE,"E10.filletArc"),sQuery(id+"F1.wireOp",EDGE,"E11.filletArc"),sQuery(id+"F1.wireOp",EDGE,"E14"),subQ3,subQ4,sQuery(id+"F1.wireOp",EDGE,"E17"),sQuery(id+"F1.wireOp",EDGE,"E18"),subQ1])],"isStart":false})});}
            extrude(context, id + "F28", {"entities" : qUnion([Q0, Q1]), "operationType" : NewBodyOperationType.REMOVE, "oppositeDirection" : true, "depth" : 12 * mm, "endBoundEntityFace" : qUnion([Q2]), "offsetDistance" : 25 * mm});
        }
    });
